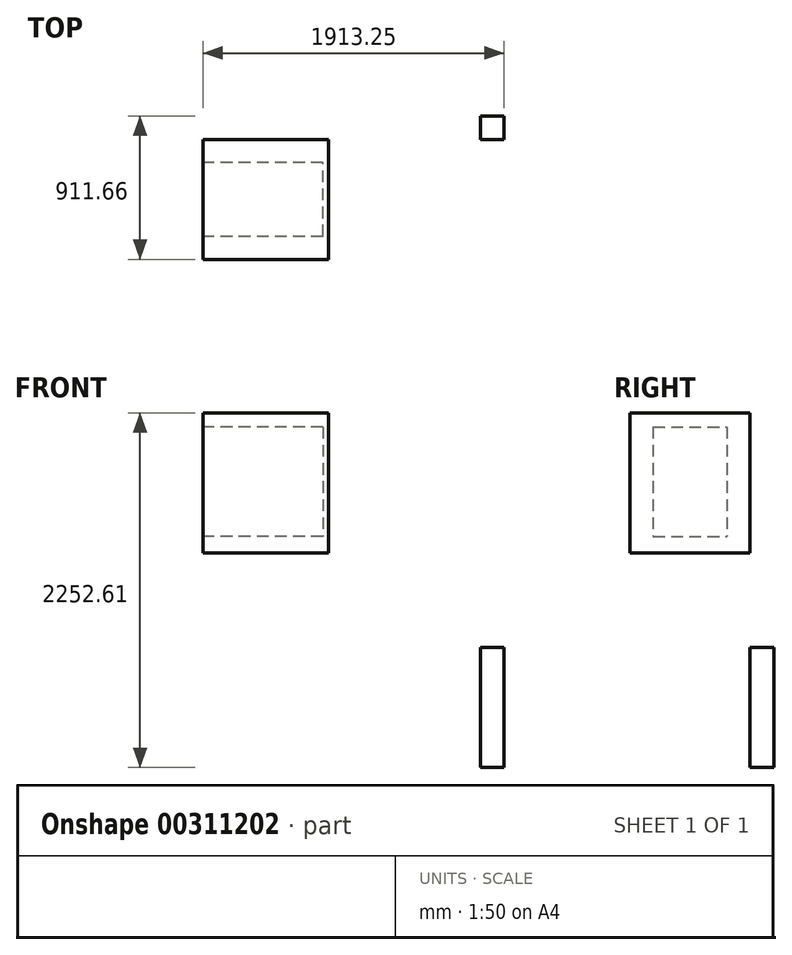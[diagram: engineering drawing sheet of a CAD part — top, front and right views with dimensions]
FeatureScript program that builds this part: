
annotation { "Feature Type Name" : "Feature", "Feature Type Description" : "" }
export const myFeature = defineFeature(function(context is Context, id is Id, definition is map)
    precondition{}
    {
        {
            var Q0;
            Q0=qCreatedBy(makeId("Top.planeOp"),FACE);
            var sketch = newSketch(context, id + "F0", { "sketchPlane" : qUnion([Q0])});
            skLineSegment(sketch, "E0.bottom", {"start": v(-75.6, -74.43) * mm, "end": v(75.55, -74.43) * mm});
            skLineSegment(sketch, "E0.top", {"start": v(-75.6, 75.23) * mm, "end": v(75.55, 75.23) * mm});
            skLineSegment(sketch, "E0.left", {"start": v(-75.6, -74.43) * mm, "end": v(-75.6, 75.23) * mm});
            skLineSegment(sketch, "E0.right", {"start": v(75.55, -74.43) * mm, "end": v(75.55, 75.23) * mm});
            skSolve(sketch);
        }
        {
            var Q0;
            Q0=makeQuery(id+"F0.imprint","IMPRINT",FACE,{"disambiguationData":[TD([[makeQuery(id+"F0.imprint","IMPRINT",EDGE,{"derivedFrom":sQuery(id+"F0.wireOp",EDGE,"E0.bottom")}),1.0]])]});
            extrude(context, id + "F1", {"entities" : qUnion([Q0]), "depth" : 762 * mm});
        }
        {
            var Q0;
            Q0=makeQuery(id+"F1.opExtrude","SWEPT_FACE",FACE,{"disambiguationData":[OSD([sQuery(id+"F0.wireOp",EDGE,"E0.bottom")])]});
            var sketch = newSketch(context, id + "F2", { "sketchPlane" : qUnion([Q0])});
            skCircle(sketch, "E1", {"center": v(-408.27, 407.32) * mm, "radius": 262.48 * mm});
            skSolve(sketch);
        }
        {
            var Q0;
            Q0=sQuery(id+"F2.wireOp",EDGE,"E1");
            extrude(context, id + "F3", {"bodyType" : ToolBodyType.SURFACE, "surfaceEntities" : qUnion([Q0]), "oppositeDirection" : true, "depth" : 147.32 * mm});
        }
        {
            var Q0;
            Q0=makeQuery(id+"F1.opExtrude","SWEPT_FACE",FACE,{"disambiguationData":[OSD([sQuery(id+"F0.wireOp",EDGE,"E0.bottom")])]});
            var sketch = newSketch(context, id + "F4", { "sketchPlane" : qUnion([Q0])});
            skSolve(sketch);
        }
        {
            var Q0;
            {var subQ0=sQuery(id+"F0.wireOp",EDGE,"E0.bottom");Q0=makeQuery(id+"F4.imprint","IMPRINT",FACE,{"disambiguationData":[TD([[makeQuery(id+"F4.imprint","IMPRINT",EDGE,{"derivedFrom":makeQuery(id+"F1.opExtrude","CAP_EDGE",EDGE,{"disambiguationData":[OSD([subQ0])],"isStart":true})}),1.0]])]});}
            var sketch = newSketch(context, id + "F5", { "sketchPlane" : qUnion([Q0])});
            skLineSegment(sketch, "E2.bottom", {"start": v(-962.48, 286.61) * mm, "end": v(-664.42, 286.61) * mm});
            skLineSegment(sketch, "E2.top", {"start": v(-962.48, 0) * mm, "end": v(-664.42, 0) * mm});
            skLineSegment(sketch, "E2.left", {"start": v(-962.48, 286.61) * mm, "end": v(-962.48, 0) * mm});
            skLineSegment(sketch, "E2.right", {"start": v(-664.42, 286.61) * mm, "end": v(-664.42, 0) * mm});
            skSolve(sketch);
        }
        {
            var Q0;
            Q0=makeQuery(id+"F5.imprint","IMPRINT",FACE,{"disambiguationData":[TD([[makeQuery(id+"F5.imprint","IMPRINT",EDGE,{"derivedFrom":sQuery(id+"F5.wireOp",EDGE,"E2.bottom")}),-1.0]])]});
            var sketch = newSketch(context, id + "F6", { "sketchPlane" : qUnion([Q0])});
            skLineSegment(sketch, "E3.bottom", {"start": v(-1039.44, 2252.61) * mm, "end": v(-1837.7, 2252.61) * mm});
            skLineSegment(sketch, "E3.top", {"start": v(-1039.44, 1363.23) * mm, "end": v(-1837.7, 1363.23) * mm});
            skLineSegment(sketch, "E3.left", {"start": v(-1039.44, 2252.61) * mm, "end": v(-1039.44, 1363.23) * mm});
            skLineSegment(sketch, "E3.right", {"start": v(-1837.7, 2252.61) * mm, "end": v(-1837.7, 1363.23) * mm});
            skSolve(sketch);
        }
        {
            var Q0;
            Q0=makeQuery(id+"F6.imprint","IMPRINT",FACE,{"disambiguationData":[TD([[makeQuery(id+"F6.imprint","IMPRINT",EDGE,{"derivedFrom":sQuery(id+"F6.wireOp",EDGE,"E3.bottom")}),1.0]])]});
            extrude(context, id + "F7", {"entities" : qUnion([Q0]), "depth" : 762 * mm});
        }
        {
            var Q0;
            Q0=makeQuery(id+"F7.opExtrude","SWEPT_FACE",FACE,{"disambiguationData":[OSD([sQuery(id+"F6.wireOp",EDGE,"E3.right")])]});
            var sketch = newSketch(context, id + "F8", { "sketchPlane" : qUnion([Q0])});
            skLineSegment(sketch, "E4.bottom", {"start": v(690.55, 2164.62) * mm, "end": v(221.85, 2164.62) * mm});
            skLineSegment(sketch, "E4.top", {"start": v(690.55, 1468.22) * mm, "end": v(221.85, 1468.22) * mm});
            skLineSegment(sketch, "E4.left", {"start": v(690.55, 2164.62) * mm, "end": v(690.55, 1468.22) * mm});
            skLineSegment(sketch, "E4.right", {"start": v(221.85, 2164.62) * mm, "end": v(221.85, 1468.22) * mm});
            skSolve(sketch);
        }
        {
            var Q0;
            Q0=makeQuery(id+"F8.imprint","IMPRINT",FACE,{"disambiguationData":[TD([[makeQuery(id+"F8.imprint","IMPRINT",EDGE,{"derivedFrom":sQuery(id+"F8.wireOp",EDGE,"E4.bottom")}),1.0]])]});
            extrude(context, id + "F9", {"entities" : qUnion([Q0]), "operationType" : NewBodyOperationType.REMOVE, "oppositeDirection" : true, "depth" : 762 * mm});
        }
    });
